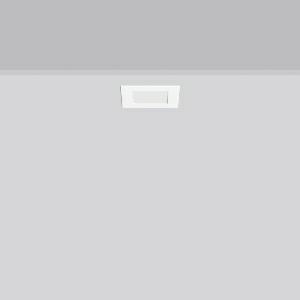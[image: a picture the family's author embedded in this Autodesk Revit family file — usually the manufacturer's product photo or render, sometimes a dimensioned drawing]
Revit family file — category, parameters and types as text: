
# Revit family: toledo_flat_square_e_672233_002_da05
name_source: partatom
category: Lighting Fixtures
units: mm (PartAtom-declared; Revit-internal decimal feet)

## family parameters
Cut with Voids When Loaded = No
Host = Face
Light Source = No
Part Type = Normal
Room Calculation Point = No
Round Connector Dimension = Use Diameter
Shared = No

## types (1)
- TOLEDO FLAT square E (1 x LED Modul 830, 370 lm, 3000)
    Apparent Load = 7 VA
    CIE Flux Codes = 49 80 96 100 100
    Color Rendering = 80
    Color Temperature = 3000
    Default Elevation = 1800 mm
    Description = Series: TOLEDO FLAT square
Square recessed downlight. For escape route illumination. Housing: die-cast aluminium, powder-coated. Lightguide and diffuser made of non-yellowing plastic (PMMA). Diffuser opal matt plastic. Ceiling installation with spring system. Including separate LED converter with connecting cable 250 mm. Self-contained system with automatic self-test. External driver with simple plug-in locking system. 
Colour: white
Length: 110 mm
Width: 110 mm
Height: 3 mm
Cut-out length: 96 mm
Cut-out width: 96 mm
Recess height: 170 mm
Luminaire: recess height: 60-80 mm
Weight: 1.25 kg
Operating mode: maintained power mode
Duration time: 3 h
Lamp: LED
Socket: without socket
Colour temperature: 3000K
Colour rendering index (CRI): 80
System power: 7.2 W
Rated luminous flux: 370 lm
Luminous flux, emergency: 280 lm
System power, emergency: -
Control gear: Regulated power supply
Protection class: I
Type of protection: IP 54
    Height = 0 mm  [stored 0 ft]
    Lamp = 1 x LED Modul 830
    Lamp Light Flux = 370 lm
    Lamp count = 1
    Length = 110 mm
    Lifetime = 50000 h
    Luminous efficacy = 51 lm/W
    Manufacturer = RZB
    ModVariant = No
    Model = 672233.002
    Mounting Place = Ceiling
    Mounting Type = Recessed
    Number of Poles = 1
    OnlyDefault = Yes
    Power Factor = 1
    Product Name = TOLEDO FLAT square E
    Product group = Recessed downlights
    ProductGroupID = 402
    Protection Class = Protection class I
    Protection Degree = IP 40
    RLX_Detail_Level = 1
    RLX_Emergency_Light_Flux = 280 lm
    RLX_Emergency_Type = 3
    RLX_Emergency_Type_DB = Yes
    RlxData = <blob elided: 9629 chars, md5=88ff2192>
    Socket = socket
    Standby Power = 0 W
    System Light Flux = 370 lm
    System Power = 7 W
    Type Comments = Product without accessories
    Type Image = 901485.002.jpg
    URL = http://relux.com
    VarID = ---
    Voltage = 0 V
    Weight = 0.00 kg
    Width = 110 mm

note: [stored X ft] marks values corroborated as IEEE doubles in the binary element streams (Revit-internal decimal feet)

## geometry (parser evidence)
native form markers: Sweep x10
no freeform markers — native parametric forms only
